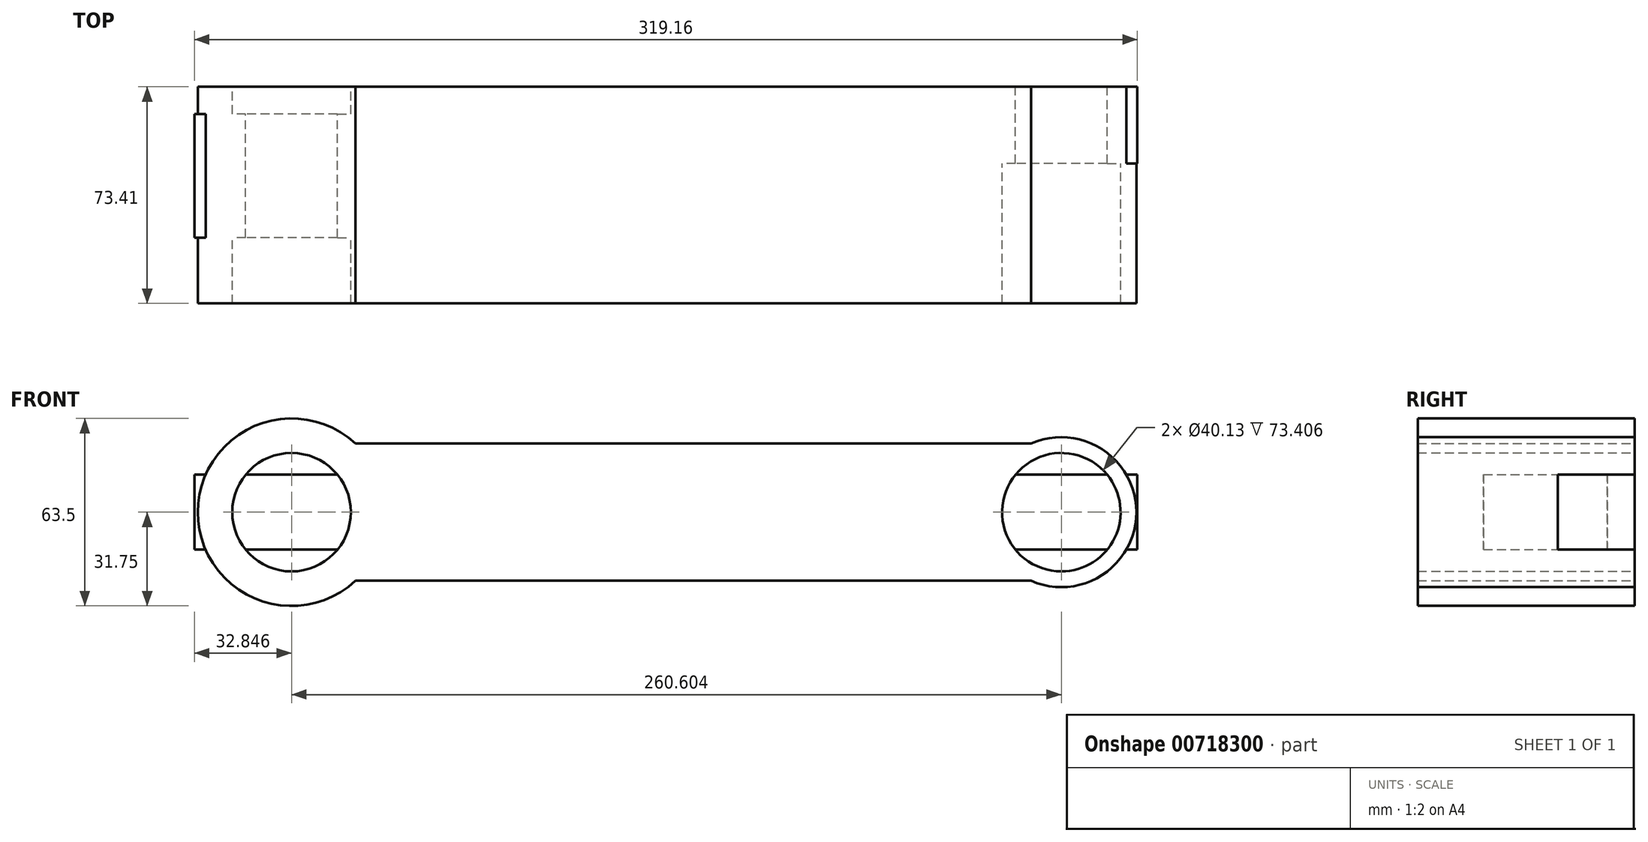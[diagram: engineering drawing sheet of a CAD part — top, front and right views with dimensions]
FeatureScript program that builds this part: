
annotation { "Feature Type Name" : "Feature", "Feature Type Description" : "" }
export const myFeature = defineFeature(function(context is Context, id is Id, definition is map)
    precondition{}
    {
        {
            var Q0;
            Q0=qCreatedBy(makeId("Front.planeOp"),FACE);
            var sketch = newSketch(context, id + "F0", { "sketchPlane" : qUnion([Q0])});
            skCircle(sketch, "E0", {"center": v(0, 0) * mm, "radius": 25.4 * mm});
            skCircle(sketch, "E1", {"center": v(-260.6, 0) * mm, "radius": 31.75 * mm});
            skLineSegment(sketch, "E2", {"start": v(-260.6, 0) * mm, "end": v(0, 0) * mm, "construction": true});
            skLineSegment(sketch, "E3", {"start": v(-238.97, 23.24) * mm, "end": v(-10.25, 23.24) * mm});
            skLineSegment(sketch, "E4.MirrorCS", {"start": v(-238.97, -23.24) * mm, "end": v(-10.25, -23.24) * mm});
            skCircle(sketch, "E5", {"center": v(-260.6, 0) * mm, "radius": 20.07 * mm});
            skCircle(sketch, "E6", {"center": v(0, 0) * mm, "radius": 20.07 * mm});
            skSolve(sketch);
        }
        {
            var Q0;
            {var subQ0=sQuery(id+"F0.wireOp",EDGE,"E3");Q0=makeQuery(id+"F0.imprint","IMPRINT",FACE,{"disambiguationData":[TD([[makeQuery(id+"F0.imprint","IMPRINT",EDGE,{"derivedFrom":subQ0}),-1.0]])]});}
            var Q1;
            Q1=makeQuery(id+"F0.imprint","IMPRINT",FACE,{"disambiguationData":[TD([[makeQuery(id+"F0.imprint","IMPRINT",EDGE,{"derivedFrom":sQuery(id+"F0.wireOp",EDGE,"E5")}),-1.0]])]});
            var Q2;
            Q2=makeQuery(id+"F0.imprint","IMPRINT",FACE,{"disambiguationData":[TD([[makeQuery(id+"F0.imprint","IMPRINT",EDGE,{"derivedFrom":sQuery(id+"F0.wireOp",EDGE,"E6")}),-1.0]])]});
            extrude(context, id + "F1", {"entities" : qUnion([Q0, Q1, Q2]), "depth" : 25.4 * mm, "offsetDistance" : 25.4 * mm});
        }
        {
            var Q0;
            Q0=makeQuery(id+"F1.opExtrude","CAP_FACE",FACE,{"disambiguationData":[OSD([sQuery(id+"F0.wireOp",EDGE,"E0"),sQuery(id+"F0.wireOp",EDGE,"E1"),sQuery(id+"F0.wireOp",EDGE,"E3"),sQuery(id+"F0.wireOp",EDGE,"E4.MirrorCS"),sQuery(id+"F0.wireOp",EDGE,"E5"),sQuery(id+"F0.wireOp",EDGE,"E6")])],"isStart":false});
            extrude(context, id + "F2", {"entities" : qUnion([Q0]), "operationType" : NewBodyOperationType.ADD, "depth" : 48 * mm, "offsetDistance" : 25.4 * mm});
        }
        {
            var Q0;
            Q0=qCreatedBy(makeId("Top.planeOp"),FACE);
            var sketch = newSketch(context, id + "F3", { "sketchPlane" : qUnion([Q0])});
            skLineSegment(sketch, "E7", {"start": v(-163.88, 0) * mm, "end": v(-188.48, -9.25) * mm});
            skLineSegment(sketch, "E8", {"start": v(-188.48, -9.25) * mm, "end": v(-316.78, -9.25) * mm});
            skLineSegment(sketch, "E9.0", {"start": v(-180.86, -51.16) * mm, "end": v(-316.78, -51.16) * mm});
            skLineSegment(sketch, "E9.1", {"start": v(-113.81, -25.95) * mm, "end": v(-180.86, -51.16) * mm});
            skLineSegment(sketch, "E10", {"start": v(-163.88, 0) * mm, "end": v(25.71, 0) * mm});
            skLineSegment(sketch, "E11", {"start": v(25.71, 0) * mm, "end": v(25.71, -25.95) * mm});
            skLineSegment(sketch, "E12", {"start": v(25.71, -25.95) * mm, "end": v(-113.81, -25.95) * mm});
            skLineSegment(sketch, "E13", {"start": v(-293.45, -51.16) * mm, "end": v(-316.78, -51.16) * mm});
            skLineSegment(sketch, "E14", {"start": v(-293.45, -51.16) * mm, "end": v(-293.45, -9.25) * mm});
            skLineSegment(sketch, "E15", {"start": v(-316.78, -9.25) * mm, "end": v(-293.45, -9.25) * mm});
            skLineSegment(sketch, "E16", {"start": v(-292.35, -73.4) * mm, "end": v(-292.35, 0) * mm});
            skLineSegment(sketch, "E17.1.0", {"start": v(-10.25, 0) * mm, "end": v(25.4, 0) * mm});
            skLineSegment(sketch, "E17.1.1", {"start": v(-10.25, 0) * mm, "end": v(-10.25, -73.4) * mm});
            skLineSegment(sketch, "E17.1.2", {"start": v(-10.25, -73.4) * mm, "end": v(25.4, -73.4) * mm});
            skLineSegment(sketch, "E17.1.3", {"start": v(-10.25, -73.4) * mm, "end": v(-10.25, 0) * mm});
            skSolve(sketch);
        }
        {
            var Q0;
            Q0 = qSketchRegion(id + "F3", true);
            extrude(context, id + "F4", {"entities" : qUnion([Q0]), "operationType" : NewBodyOperationType.ADD, "endBound" : BoundingType.SYMMETRIC, "depth" : 25.4 * mm, "offsetDistance" : 25.4 * mm});
        }
    });
